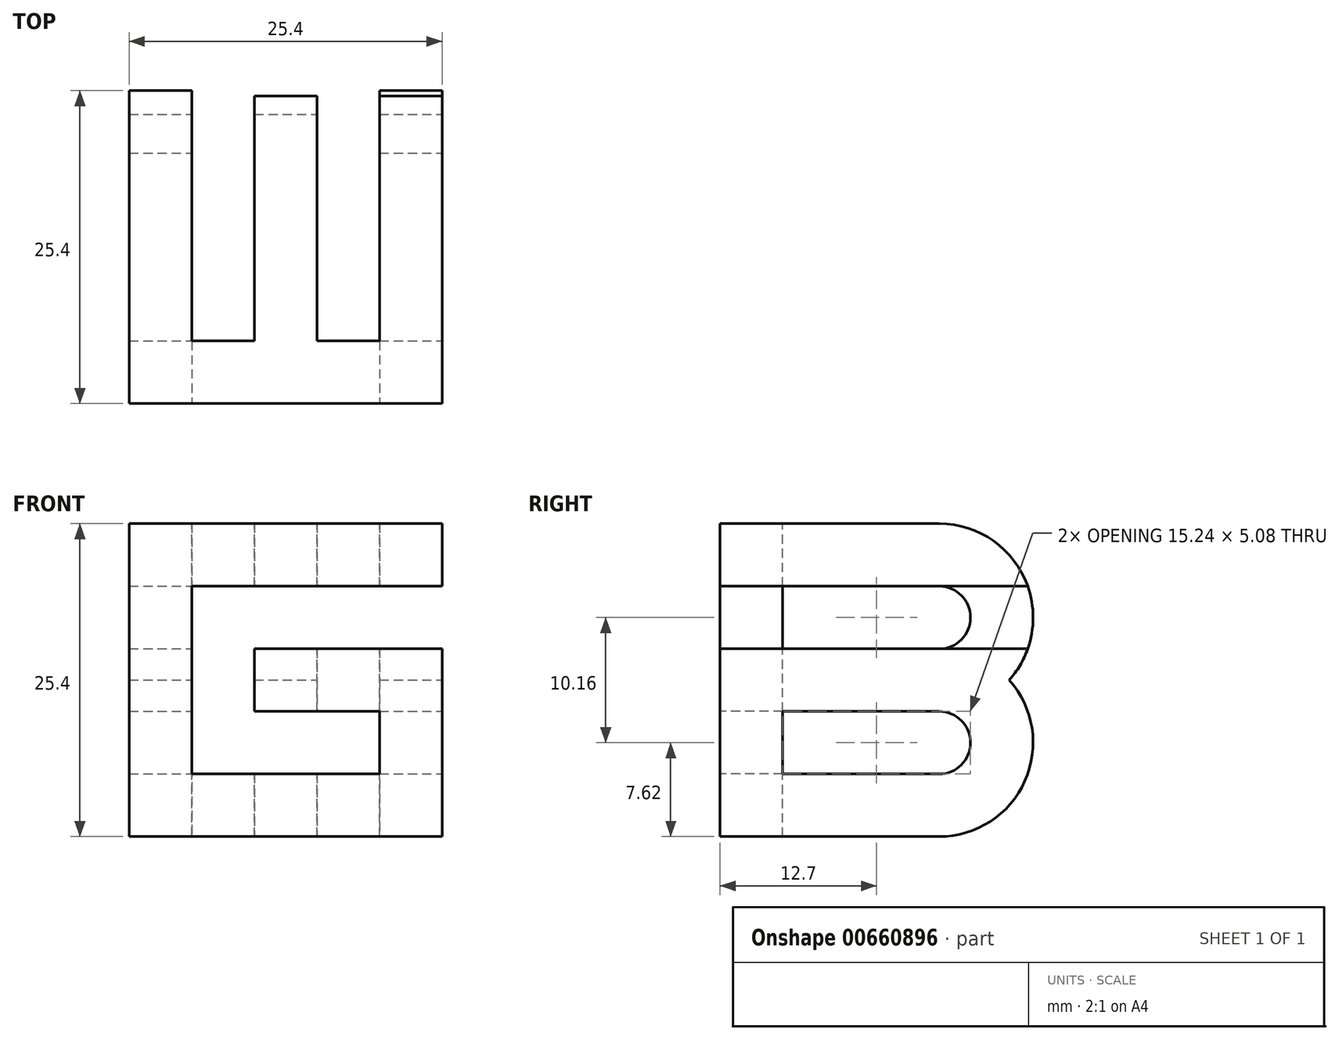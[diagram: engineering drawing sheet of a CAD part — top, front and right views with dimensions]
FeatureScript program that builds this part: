
annotation { "Feature Type Name" : "Feature", "Feature Type Description" : "" }
export const myFeature = defineFeature(function(context is Context, id is Id, definition is map)
    precondition{}
    {
        {
            var Q0;
            Q0=qCreatedBy(makeId("Top.planeOp"),FACE);
            var sketch = newSketch(context, id + "F0", { "sketchPlane" : qUnion([Q0])});
            skLineSegment(sketch, "E0.bottom", {"start": v(12.7, -12.7) * mm, "end": v(-12.7, -12.7) * mm});
            skLineSegment(sketch, "E0.top", {"start": v(12.7, 12.7) * mm, "end": v(-12.7, 12.7) * mm});
            skLineSegment(sketch, "E0.left", {"start": v(12.7, -12.7) * mm, "end": v(12.7, 12.7) * mm});
            skLineSegment(sketch, "E0.right", {"start": v(-12.7, -12.7) * mm, "end": v(-12.7, 12.7) * mm});
            skPoint(sketch, "E0.middle", {"position": v(0, 0) * mm});
            skSolve(sketch);
        }
        {
            var Q0;
            Q0=makeQuery(id+"F0.imprint","IMPRINT",FACE,{"disambiguationData":[TD([[makeQuery(id+"F0.imprint","IMPRINT",EDGE,{"derivedFrom":sQuery(id+"F0.wireOp",EDGE,"E0.bottom")}),-1.0]])]});
            extrude(context, id + "F1", {"entities" : qUnion([Q0]), "depth" : 25.4 * mm, "offsetDistance" : 25.4 * mm});
        }
        {
            var Q0;
            Q0=makeQuery(id+"F1.opExtrude","CAP_FACE",FACE,{"disambiguationData":[OSD([sQuery(id+"F0.wireOp",EDGE,"E0.bottom"),sQuery(id+"F0.wireOp",EDGE,"E0.top"),sQuery(id+"F0.wireOp",EDGE,"E0.left"),sQuery(id+"F0.wireOp",EDGE,"E0.right")])],"isStart":false});
            var sketch = newSketch(context, id + "F2", { "sketchPlane" : qUnion([Q0])});
            skLineSegment(sketch, "E1.bottom", {"start": v(-7.62, 12.7) * mm, "end": v(-2.54, 12.7) * mm});
            skLineSegment(sketch, "E1.top", {"start": v(-7.62, -7.62) * mm, "end": v(-2.54, -7.62) * mm});
            skLineSegment(sketch, "E1.left", {"start": v(-7.62, 12.7) * mm, "end": v(-7.62, -7.62) * mm});
            skLineSegment(sketch, "E1.right", {"start": v(-2.54, 12.7) * mm, "end": v(-2.54, -7.62) * mm});
            skLineSegment(sketch, "E2.bottom", {"start": v(2.54, 12.7) * mm, "end": v(7.62, 12.7) * mm});
            skLineSegment(sketch, "E2.top", {"start": v(2.54, -7.62) * mm, "end": v(7.62, -7.62) * mm});
            skLineSegment(sketch, "E2.left", {"start": v(2.54, 12.7) * mm, "end": v(2.54, -7.62) * mm});
            skLineSegment(sketch, "E2.right", {"start": v(7.62, 12.7) * mm, "end": v(7.62, -7.62) * mm});
            skSolve(sketch);
        }
        {
            var Q0;
            Q0=makeQuery(id+"F2.imprint","IMPRINT",FACE,{"disambiguationData":[TD([[makeQuery(id+"F2.imprint","IMPRINT",EDGE,{"derivedFrom":sQuery(id+"F2.wireOp",EDGE,"E1.bottom")}),1.0]])]});
            var Q1;
            Q1=makeQuery(id+"F2.imprint","IMPRINT",FACE,{"disambiguationData":[TD([[makeQuery(id+"F2.imprint","IMPRINT",EDGE,{"derivedFrom":sQuery(id+"F2.wireOp",EDGE,"E2.bottom")}),1.0]])]});
            extrude(context, id + "F3", {"entities" : qUnion([Q0, Q1]), "operationType" : NewBodyOperationType.REMOVE, "oppositeDirection" : true, "depth" : 25.4 * mm, "offsetDistance" : 25.4 * mm});
        }
        {
            var Q0;
            Q0=makeQuery(id+"F1.opExtrude","SWEPT_FACE",FACE,{"disambiguationData":[OSD([sQuery(id+"F0.wireOp",EDGE,"E0.left")])]});
            var sketch = newSketch(context, id + "F4", { "sketchPlane" : qUnion([Q0])});
            skLineSegment(sketch, "E3.bottom", {"start": v(-7.62, 20.32) * mm, "end": v(5.08, 20.32) * mm});
            skLineSegment(sketch, "E3.top", {"start": v(-7.62, 15.24) * mm, "end": v(5.08, 15.24) * mm});
            skLineSegment(sketch, "E3.left", {"start": v(-7.62, 20.32) * mm, "end": v(-7.62, 15.24) * mm});
            skLineSegment(sketch, "E4.bottom", {"start": v(-7.62, 10.16) * mm, "end": v(5.08, 10.16) * mm});
            skLineSegment(sketch, "E4.top", {"start": v(-7.62, 5.08) * mm, "end": v(5.08, 5.08) * mm});
            skLineSegment(sketch, "E4.left", {"start": v(-7.62, 10.16) * mm, "end": v(-7.62, 5.08) * mm});
            skArc(sketch, "E5", {"start": v(5.08, 20.32) * mm, "mid": v(7.62, 17.78) * mm, "end": v(5.08, 15.24) * mm});
            skArc(sketch, "E6", {"start": v(5.08, 10.16) * mm, "mid": v(7.62, 7.62) * mm, "end": v(5.08, 5.08) * mm});
            skArc(sketch, "E7", {"start": v(5.08, 0) * mm, "mid": v(12.04, 4.5) * mm, "end": v(10.76, 12.7) * mm});
            skLineSegment(sketch, "E8.0", {"start": v(-12.7, 25.4) * mm, "end": v(12.7, 25.4) * mm});
            skArc(sketch, "E9.trimOffspring", {"start": v(10.76, 12.7) * mm, "mid": v(12.04, 20.9) * mm, "end": v(5.08, 25.4) * mm});
            skLineSegment(sketch, "E10.0", {"start": v(-12.7, 0) * mm, "end": v(12.7, 0) * mm});
            skSolve(sketch);
        }
        {
            var Q0;
            Q0=makeQuery(id+"F4.imprint","IMPRINT",FACE,{"disambiguationData":[TD([[makeQuery(id+"F4.imprint","IMPRINT",EDGE,{"derivedFrom":sQuery(id+"F4.wireOp",EDGE,"E3.bottom")}),-1.0]])]});
            var Q1;
            Q1=makeQuery(id+"F4.imprint","IMPRINT",FACE,{"disambiguationData":[TD([[makeQuery(id+"F4.imprint","IMPRINT",EDGE,{"derivedFrom":sQuery(id+"F4.wireOp",EDGE,"E4.bottom")}),-1.0]])]});
            var Q2;
            {var subQ0=sQuery(id+"F4.wireOp",EDGE,"E8.0");var subQ3=sQuery(id+"F4.wireOp",EDGE,"E9.trimOffspring");var subQ4=makeQuery(id+"F4.imprint","INTERSECT",VERTEX,{"derivedFrom":[subQ0,subQ3]});Q2=makeQuery(id+"F4.imprint","IMPRINT",FACE,{"disambiguationData":[TD([[makeQuery(id+"F4.imprint","IMPRINT",EDGE,{"disambiguationData":[TD([[subQ4,-1.0]])],"derivedFrom":subQ0}),-1.0]])]});}
            var Q3;
            {var subQ0=sQuery(id+"F4.wireOp",EDGE,"E9.trimOffspring");var subQ1=sQuery(id+"F4.wireOp",EDGE,"E7");var subQ2=makeQuery(id+"F4.imprint","INTERSECT",VERTEX,{"derivedFrom":[subQ1,subQ0]});Q3=makeQuery(id+"F4.imprint","IMPRINT",FACE,{"disambiguationData":[TD([[makeQuery(id+"F4.imprint","IMPRINT",EDGE,{"disambiguationData":[TD([[subQ2,1.0]])],"derivedFrom":subQ1}),-1.0]])]});}
            var Q4;
            {var subQ0=sQuery(id+"F4.wireOp",EDGE,"E10.0");var subQ1=sQuery(id+"F4.wireOp",EDGE,"E7");var subQ2=makeQuery(id+"F4.imprint","INTERSECT",VERTEX,{"derivedFrom":[subQ1,subQ0]});Q4=makeQuery(id+"F4.imprint","IMPRINT",FACE,{"disambiguationData":[TD([[makeQuery(id+"F4.imprint","IMPRINT",EDGE,{"disambiguationData":[TD([[subQ2,-1.0]])],"derivedFrom":subQ1}),-1.0]])]});}
            extrude(context, id + "F5", {"entities" : qUnion([Q0, Q1, Q2, Q3, Q4]), "operationType" : NewBodyOperationType.REMOVE, "oppositeDirection" : true, "depth" : 25.4 * mm, "offsetDistance" : 25.4 * mm});
        }
        {
            var Q0;
            Q0=makeQuery(id+"F1.opExtrude","SWEPT_FACE",FACE,{"disambiguationData":[OSD([sQuery(id+"F0.wireOp",EDGE,"E0.bottom")])]});
            var sketch = newSketch(context, id + "F6", { "sketchPlane" : qUnion([Q0])});
            skLineSegment(sketch, "E11.bottom", {"start": v(12.7, 20.32) * mm, "end": v(-7.62, 20.32) * mm});
            skLineSegment(sketch, "E11.top", {"start": v(12.7, 15.24) * mm, "end": v(-2.54, 15.24) * mm});
            skLineSegment(sketch, "E11.left", {"start": v(12.7, 20.32) * mm, "end": v(12.7, 15.24) * mm});
            skLineSegment(sketch, "E11.right", {"start": v(-7.62, 20.32) * mm, "end": v(-7.62, 15.24) * mm});
            skLineSegment(sketch, "E12.top", {"start": v(-7.62, 5.08) * mm, "end": v(-2.54, 5.08) * mm});
            skLineSegment(sketch, "E12.left", {"start": v(-7.62, 15.24) * mm, "end": v(-7.62, 5.08) * mm});
            skLineSegment(sketch, "E12.right", {"start": v(-2.54, 15.24) * mm, "end": v(-2.54, 10.16) * mm});
            skLineSegment(sketch, "E13.bottom", {"start": v(-2.54, 5.08) * mm, "end": v(7.62, 5.08) * mm});
            skLineSegment(sketch, "E13.top", {"start": v(-2.54, 10.16) * mm, "end": v(7.62, 10.16) * mm});
            skLineSegment(sketch, "E13.right", {"start": v(7.62, 5.08) * mm, "end": v(7.62, 10.16) * mm});
            skSolve(sketch);
        }
        {
            var Q0;
            Q0=makeQuery(id+"F6.imprint","IMPRINT",FACE,{"disambiguationData":[TD([[makeQuery(id+"F6.imprint","IMPRINT",EDGE,{"derivedFrom":sQuery(id+"F6.wireOp",EDGE,"E11.bottom")}),1.0]])]});
            extrude(context, id + "F7", {"entities" : qUnion([Q0]), "operationType" : NewBodyOperationType.REMOVE, "oppositeDirection" : true, "depth" : 25.4 * mm, "offsetDistance" : 25.4 * mm});
        }
    });
